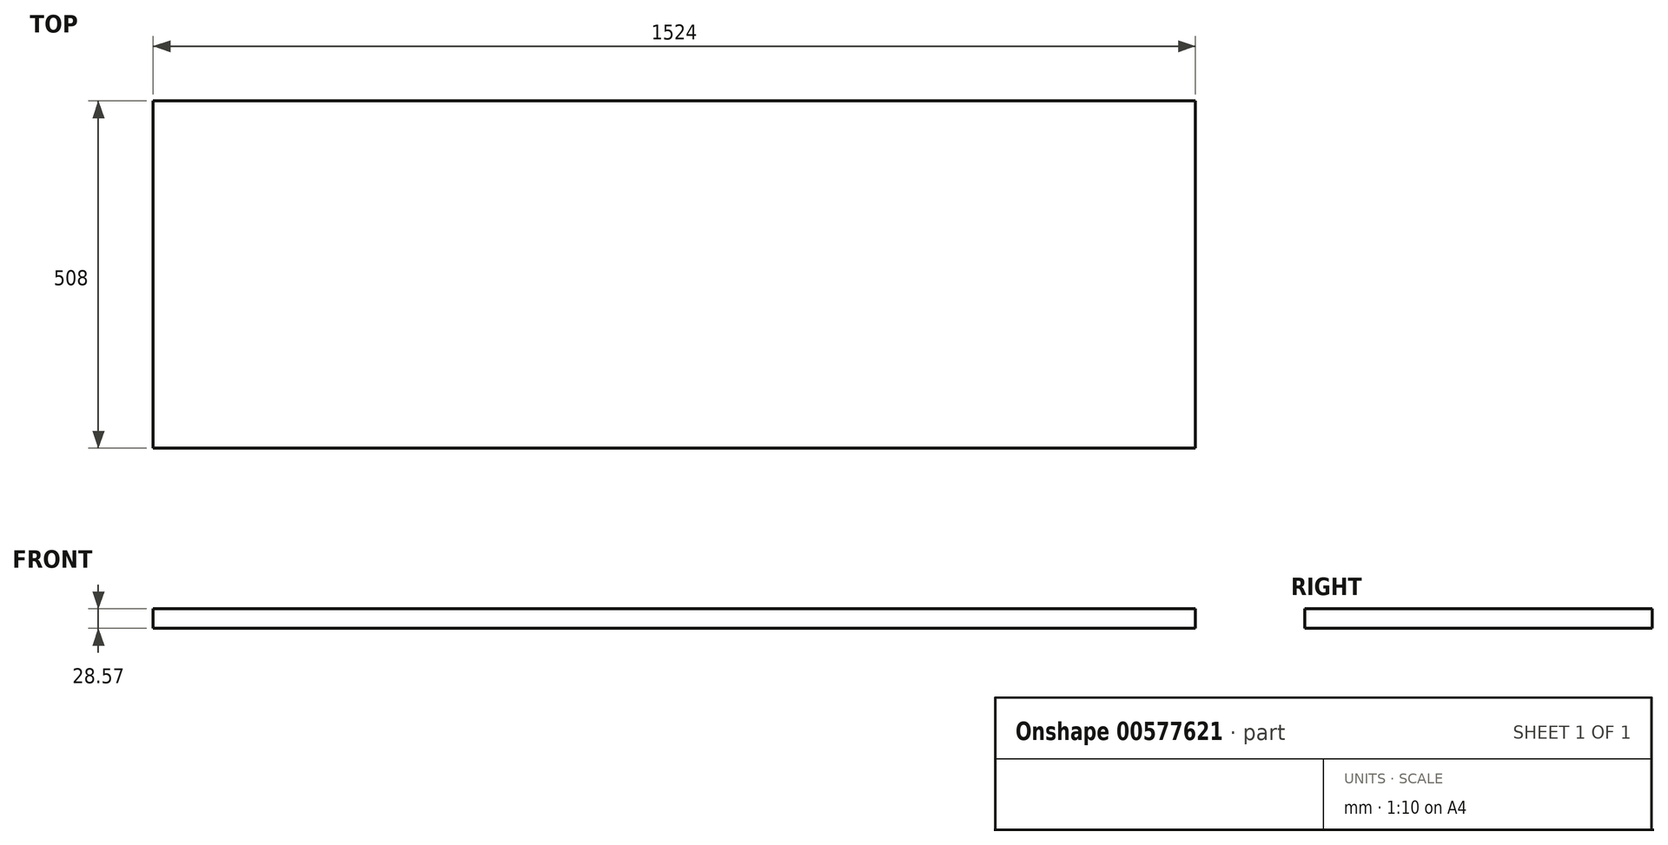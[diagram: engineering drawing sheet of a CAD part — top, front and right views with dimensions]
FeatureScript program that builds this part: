
annotation { "Feature Type Name" : "Feature", "Feature Type Description" : "" }
export const myFeature = defineFeature(function(context is Context, id is Id, definition is map)
    precondition{}
    {
        {
            var Q0;
            Q0=qCreatedBy(makeId("Top.planeOp"),FACE);
            var sketch = newSketch(context, id + "F0", { "sketchPlane" : qUnion([Q0])});
            skLineSegment(sketch, "E0.bottom", {"start": v(762, 254) * mm, "end": v(-762, 254) * mm});
            skLineSegment(sketch, "E0.top", {"start": v(762, -254) * mm, "end": v(-762, -254) * mm});
            skLineSegment(sketch, "E0.left", {"start": v(762, 254) * mm, "end": v(762, -254) * mm});
            skLineSegment(sketch, "E0.right", {"start": v(-762, 254) * mm, "end": v(-762, -254) * mm});
            skPoint(sketch, "E0.middle", {"position": v(0, 0) * mm});
            skSolve(sketch);
        }
        {
            var Q0;
            Q0=makeQuery(id+"F0.imprint","IMPRINT",FACE,{"disambiguationData":[TD([[makeQuery(id+"F0.imprint","IMPRINT",EDGE,{"derivedFrom":sQuery(id+"F0.wireOp",EDGE,"E0.bottom")}),1.0]])]});
            extrude(context, id + "F1", {"entities" : qUnion([Q0]), "depth" : 28.57 * mm, "offsetDistance" : 25.4 * mm});
        }
    });
